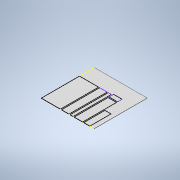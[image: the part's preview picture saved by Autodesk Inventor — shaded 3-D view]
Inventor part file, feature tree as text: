
AUTODESK INVENTOR PART (.ipt)
format: ipt  version: 2022 (Build 260153000, 153)  size: 120,320 bytes
history: native  units: mm
features: sketch x2, other x1, extrude x1
ambient origin geometry x8: Origin, YZ Plane, XZ Plane, XY Plane, X Axis, Y Axis, Z Axis, Center Point
bodies: Body1 (feature_tree)
feature tree (4):
  other  "ソリッド1"
  extrude  "押し出し1"  Depth=500.0mm
  sketch  "スケッチ2"
  sketch  "スケッチ1"
